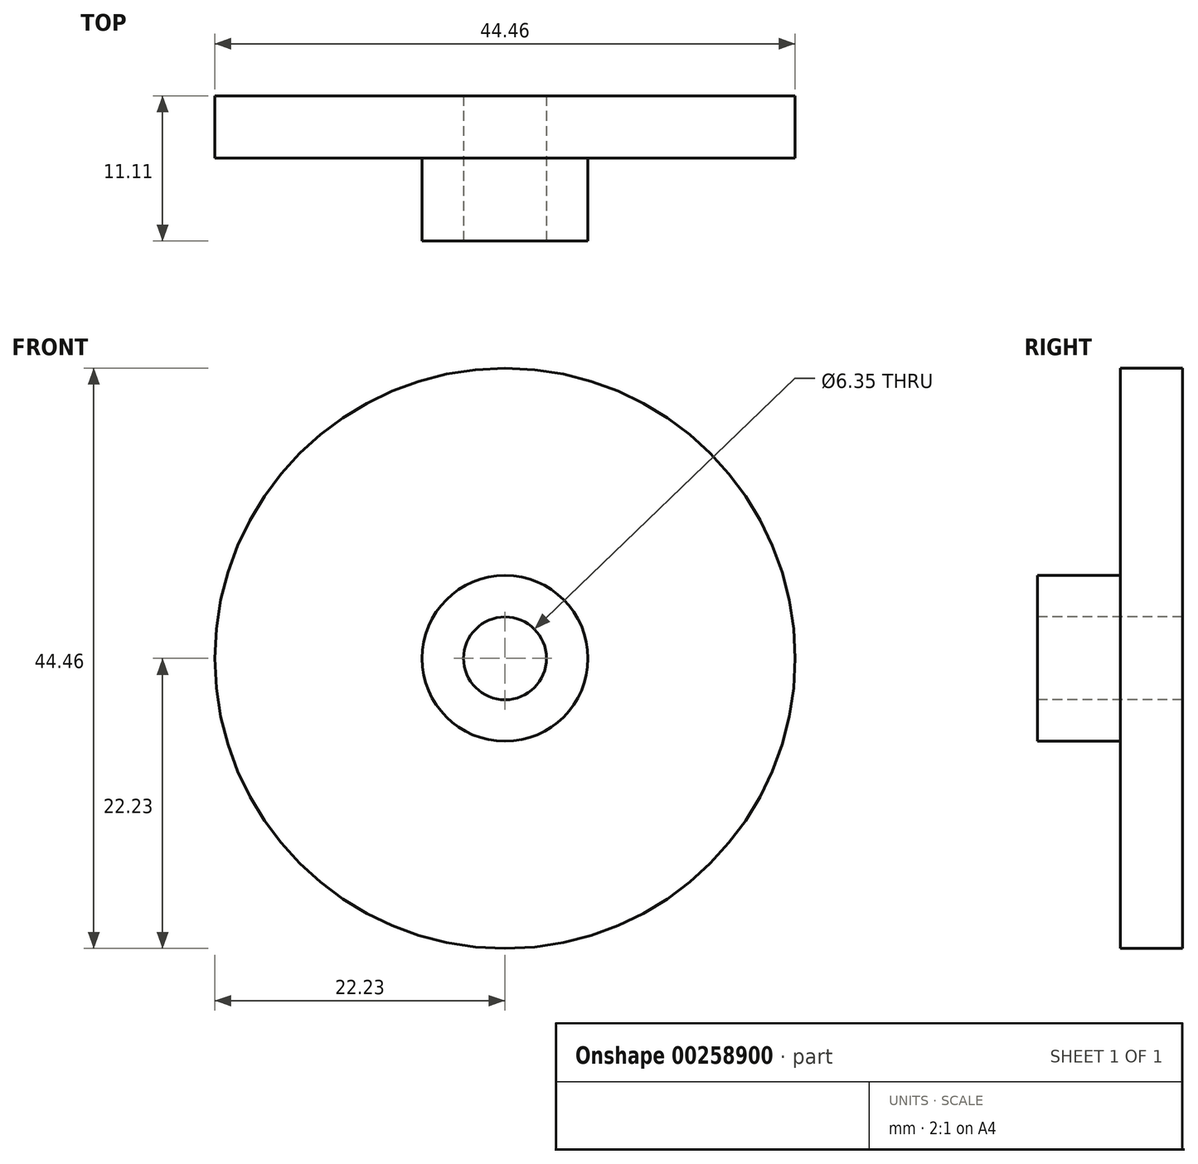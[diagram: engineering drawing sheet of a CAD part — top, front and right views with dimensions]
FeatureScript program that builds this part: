
annotation { "Feature Type Name" : "Feature", "Feature Type Description" : "" }
export const myFeature = defineFeature(function(context is Context, id is Id, definition is map)
    precondition{}
    {
        {
            var Q0;
            Q0=qCreatedBy(makeId("Front.planeOp"),FACE);
            var sketch = newSketch(context, id + "F0", { "sketchPlane" : qUnion([Q0])});
            skCircle(sketch, "E0", {"center": v(0, 0) * mm, "radius": 22.22 * mm});
            skSolve(sketch);
        }
        {
            var Q0;
            Q0=qSketchRegion(id+"F0",true);
            extrude(context, id + "F1", {"entities" : qUnion([Q0]), "depth" : 4.76 * mm});
        }
        {
            var Q0;
            Q0=makeQuery(id+"F1.opExtrude","CAP_FACE",FACE,{"disambiguationData":[OSD([sQuery(id+"F0.wireOp",EDGE,"E0")])],"isStart":false});
            var sketch = newSketch(context, id + "F2", { "sketchPlane" : qUnion([Q0])});
            skCircle(sketch, "E1", {"center": v(0, 0) * mm, "radius": 6.35 * mm});
            skSolve(sketch);
        }
        {
            var Q0;
            Q0=qSketchRegion(id+"F2",true);
            extrude(context, id + "F3", {"entities" : qUnion([Q0]), "operationType" : NewBodyOperationType.ADD, "depth" : 6.35 * mm});
        }
        {
            var Q0;
            Q0=makeQuery(id+"F3.opExtrude","CAP_FACE",FACE,{"disambiguationData":[OSD([sQuery(id+"F2.wireOp",EDGE,"E1")])],"isStart":false});
            var sketch = newSketch(context, id + "F4", { "sketchPlane" : qUnion([Q0])});
            skCircle(sketch, "E2", {"center": v(0, 0) * mm, "radius": 3.18 * mm});
            skSolve(sketch);
        }
        {
            var Q0;
            Q0=qSketchRegion(id+"F4",true);
            extrude(context, id + "F5", {"entities" : qUnion([Q0]), "operationType" : NewBodyOperationType.REMOVE, "oppositeDirection" : true, "depth" : 25.4 * mm, "hasSecondDirection" : true, "secondDirectionBound" : BoundingType.THROUGH_ALL, "secondDirectionOppositeDirection" : false, "secondDirectionDepth" : 25.4 * mm});
        }
    });
